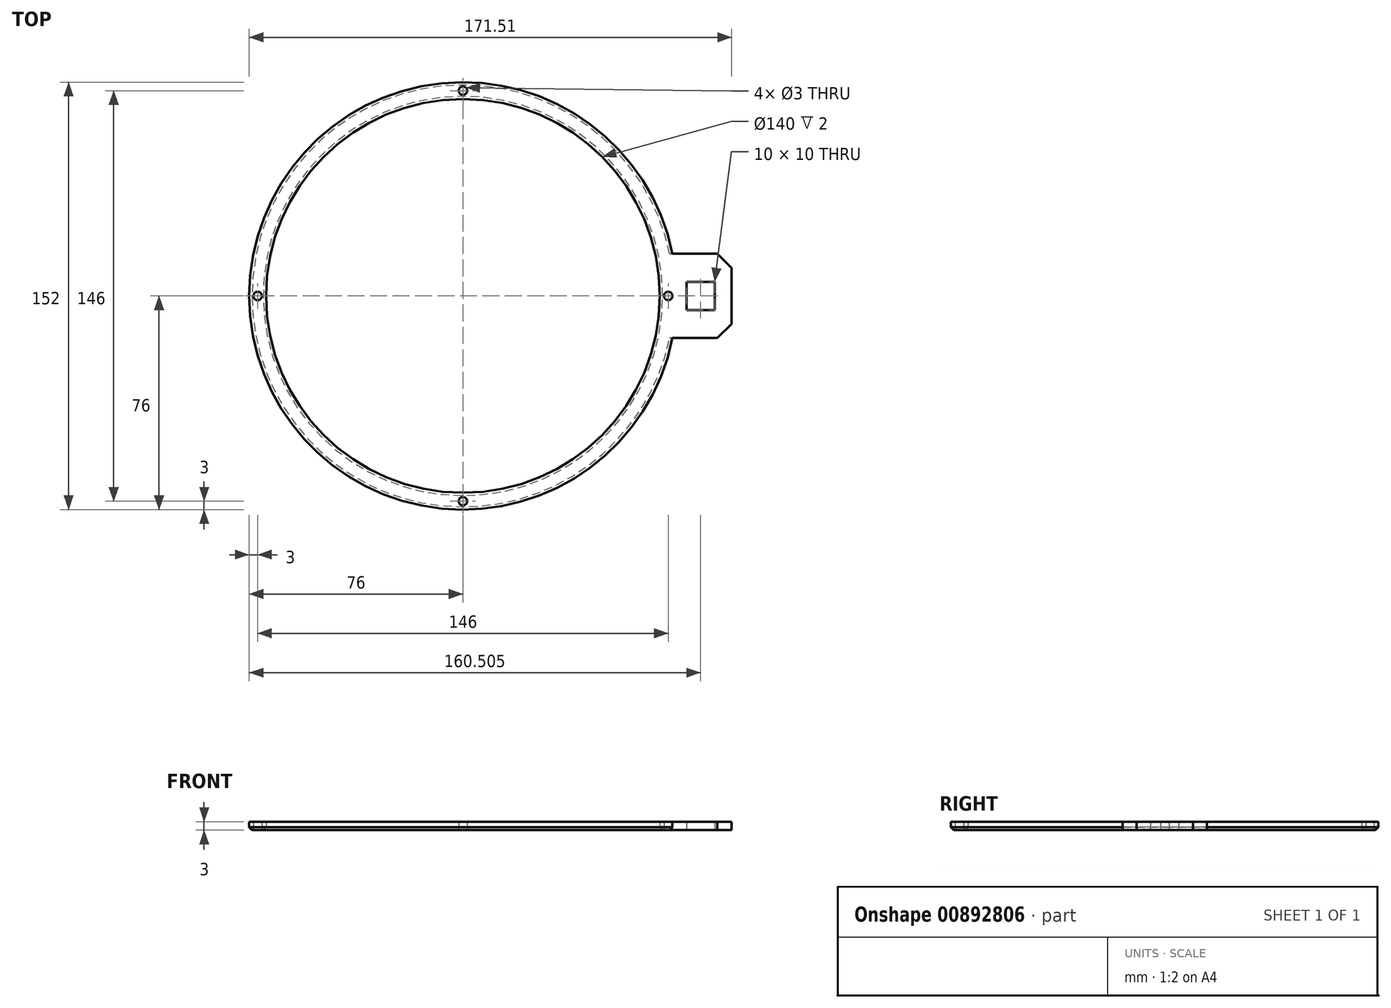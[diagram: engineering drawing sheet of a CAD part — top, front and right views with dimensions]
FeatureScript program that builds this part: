
annotation { "Feature Type Name" : "Feature", "Feature Type Description" : "" }
export const myFeature = defineFeature(function(context is Context, id is Id, definition is map)
    precondition{}
    {
        {
            var Q0;
            Q0=qCreatedBy(makeId("Top.planeOp"),FACE);
            var sketch = newSketch(context, id + "F0", { "sketchPlane" : qUnion([Q0])});
            skCircle(sketch, "E0", {"center": v(0, 0) * mm, "radius": 70 * mm});
            skPoint(sketch, "E1.start.orphan", {"position": v(70, 0) * mm});
            skLineSegment(sketch, "E2", {"start": v(70, 0) * mm, "end": v(76, 0) * mm, "construction": true});
            skArc(sketch, "E3", {"start": v(74.5, 15) * mm, "mid": v(-76, 0) * mm, "end": v(74.5, -15) * mm});
            skCircle(sketch, "E4", {"center": v(-73, 0) * mm, "radius": 1.5 * mm});
            skCircle(sketch, "E5", {"center": v(0, -73) * mm, "radius": 1.5 * mm});
            skCircle(sketch, "E6.MirrorC", {"center": v(73, 0) * mm, "radius": 1.5 * mm});
            skCircle(sketch, "E7.MirrorC", {"center": v(0, 73) * mm, "radius": 1.5 * mm});
            skPoint(sketch, "E8.orphan", {"position": v(-70, 0) * mm});
            skPoint(sketch, "E9.orphan", {"position": v(-76, 0) * mm});
            skPoint(sketch, "E10.orphan", {"position": v(0, -70) * mm});
            skPoint(sketch, "E11.orphan", {"position": v(0, -76) * mm});
            skLineSegment(sketch, "E12.bottom", {"start": v(95.5, 15) * mm, "end": v(74.5, 15) * mm});
            skLineSegment(sketch, "E12.top", {"start": v(95.5, -15) * mm, "end": v(74.5, -15) * mm});
            skPoint(sketch, "E12.right.start.orphan", {"position": v(33, 15) * mm});
            skPoint(sketch, "E13.orphan", {"position": v(33, -15) * mm});
            skLineSegment(sketch, "E14", {"start": v(74.5, 15) * mm, "end": v(79.5, 15) * mm, "construction": true});
            skLineSegment(sketch, "E15", {"start": v(79.5, 15) * mm, "end": v(79.5, -15) * mm, "construction": true});
            skPoint(sketch, "E16.orphan", {"position": v(93.75, 15) * mm});
            skPoint(sketch, "E17.end.orphan", {"position": v(93.75, 0) * mm});
            skPoint(sketch, "E17.start.orphan", {"position": v(113, 0) * mm});
            skPoint(sketch, "E18.orphan", {"position": v(93.75, -15) * mm});
            skLineSegment(sketch, "E19", {"start": v(95.5, 0) * mm, "end": v(79.5, 0) * mm, "construction": true});
            skLineSegment(sketch, "E20.bottom", {"start": v(89.5, 5) * mm, "end": v(79.5, 5) * mm});
            skLineSegment(sketch, "E20.top", {"start": v(89.5, -5) * mm, "end": v(79.5, -5) * mm});
            skLineSegment(sketch, "E20.left", {"start": v(89.5, 5) * mm, "end": v(89.5, -5) * mm});
            skPoint(sketch, "E20.middle", {"position": v(79.5, 0) * mm});
            skLineSegment(sketch, "E21", {"start": v(79.5, 5) * mm, "end": v(79.5, -5) * mm});
            skLineSegment(sketch, "E22.trimOffspring", {"start": v(69.82, 5) * mm, "end": v(69.5, 5) * mm});
            skLineSegment(sketch, "E23.trimOffspring", {"start": v(69.82, -5) * mm, "end": v(69.5, -5) * mm});
            skLineSegment(sketch, "E24", {"start": v(89.5, 0) * mm, "end": v(95.5, 0) * mm, "construction": true});
            skLineSegment(sketch, "E25", {"start": v(95.5, 0) * mm, "end": v(95.5, 15) * mm});
            skLineSegment(sketch, "E26", {"start": v(95.5, 0) * mm, "end": v(95.5, -15) * mm});
            skPoint(sketch, "E27.orphan", {"position": v(113, 15) * mm});
            skPoint(sketch, "E12.left.end.orphan", {"position": v(113, -15) * mm});
            skSolve(sketch);
        }
        {
            var Q0;
            Q0=makeQuery(id+"F0.imprint","IMPRINT",FACE,{"disambiguationData":[TD([[makeQuery(id+"F0.imprint","IMPRINT",EDGE,{"derivedFrom":sQuery(id+"F0.wireOp",EDGE,"E0")}),-1.0]])]});
            extrude(context, id + "F1", {"entities" : qUnion([Q0]), "depth" : 3 * mm, "offsetDistance" : 25 * mm});
        }
        {
            var Q0;
            Q0=makeQuery(id+"F1.opExtrude","CAP_EDGE",EDGE,{"disambiguationData":[OSD([sQuery(id+"F0.wireOp",EDGE,"E3")])],"isStart":true});
            var Q1;
            Q1=makeQuery(id+"F1.opExtrude","CAP_EDGE",EDGE,{"disambiguationData":[OSD([sQuery(id+"F0.wireOp",EDGE,"E0")])],"isStart":true});
            chamfer(context, id + "F2", {"entities" : qUnion([Q0, Q1]), "width" : 1 * mm, "tangentPropagation" : true});
        }
        {
            var Q0;
            Q0=makeQuery(id+"F1.opExtrude","SWEPT_EDGE",EDGE,{"disambiguationData":[OSD([sQuery(id+"F0.wireOp",EDGE,"E12.top"),sQuery(id+"F0.wireOp",EDGE,"E26")])]});
            var Q1;
            Q1=makeQuery(id+"F1.opExtrude","SWEPT_EDGE",EDGE,{"disambiguationData":[OSD([sQuery(id+"F0.wireOp",EDGE,"E12.bottom"),sQuery(id+"F0.wireOp",EDGE,"E25")])]});
            chamfer(context, id + "F3", {"entities" : qUnion([Q0, Q1]), "width" : 5 * mm, "tangentPropagation" : true});
        }
    });
